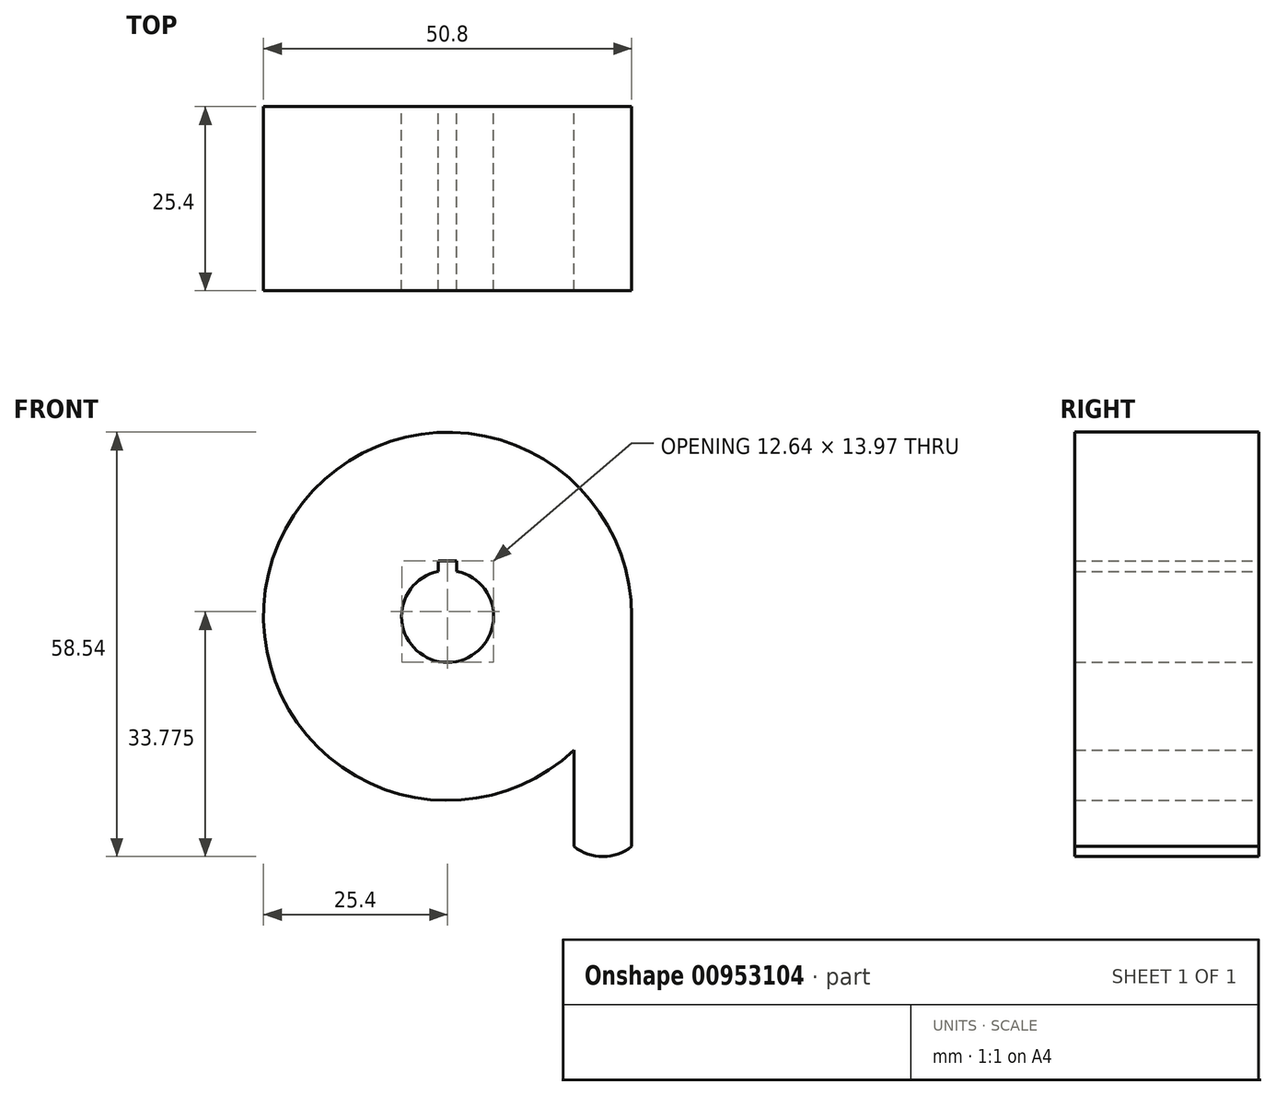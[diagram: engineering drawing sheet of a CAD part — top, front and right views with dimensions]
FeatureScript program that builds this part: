
annotation { "Feature Type Name" : "Feature", "Feature Type Description" : "" }
export const myFeature = defineFeature(function(context is Context, id is Id, definition is map)
    precondition{}
    {
        {
            var Q0;
            Q0=qCreatedBy(makeId("Front.planeOp"),FACE);
            var sketch = newSketch(context, id + "F0", { "sketchPlane" : qUnion([Q0])});
            skCircle(sketch, "E0", {"center": v(0, 0) * mm, "radius": 25.4 * mm});
            skLineSegment(sketch, "E1", {"start": v(17.46, -18.45) * mm, "end": v(17.46, -31.75) * mm});
            skLineSegment(sketch, "E2", {"start": v(25.4, 0) * mm, "end": v(25.4, -31.75) * mm});
            skArc(sketch, "E3", {"start": v(17.46, -31.75) * mm, "mid": v(21.43, -33.14) * mm, "end": v(25.4, -31.75) * mm});
            skCircle(sketch, "E4", {"center": v(0, 0) * mm, "radius": 6.35 * mm});
            skLineSegment(sketch, "E5.bottom", {"start": v(-1.27, 7.62) * mm, "end": v(1.27, 7.62) * mm});
            skLineSegment(sketch, "E5.top", {"start": v(-1.27, 5.08) * mm, "end": v(1.27, 5.08) * mm});
            skLineSegment(sketch, "E5.left", {"start": v(-1.27, 7.62) * mm, "end": v(-1.27, 5.08) * mm});
            skLineSegment(sketch, "E5.right", {"start": v(1.27, 7.62) * mm, "end": v(1.27, 5.08) * mm});
            skPoint(sketch, "E5.middle", {"position": v(0, 6.35) * mm});
            skSolve(sketch);
        }
        {
            var Q0;
            Q0 = qSketchRegion(id + "F0", true);
            extrude(context, id + "F1", {"entities" : qUnion([Q0]), "depth" : 25.4 * mm, "offsetDistance" : 25.4 * mm});
        }
    });
